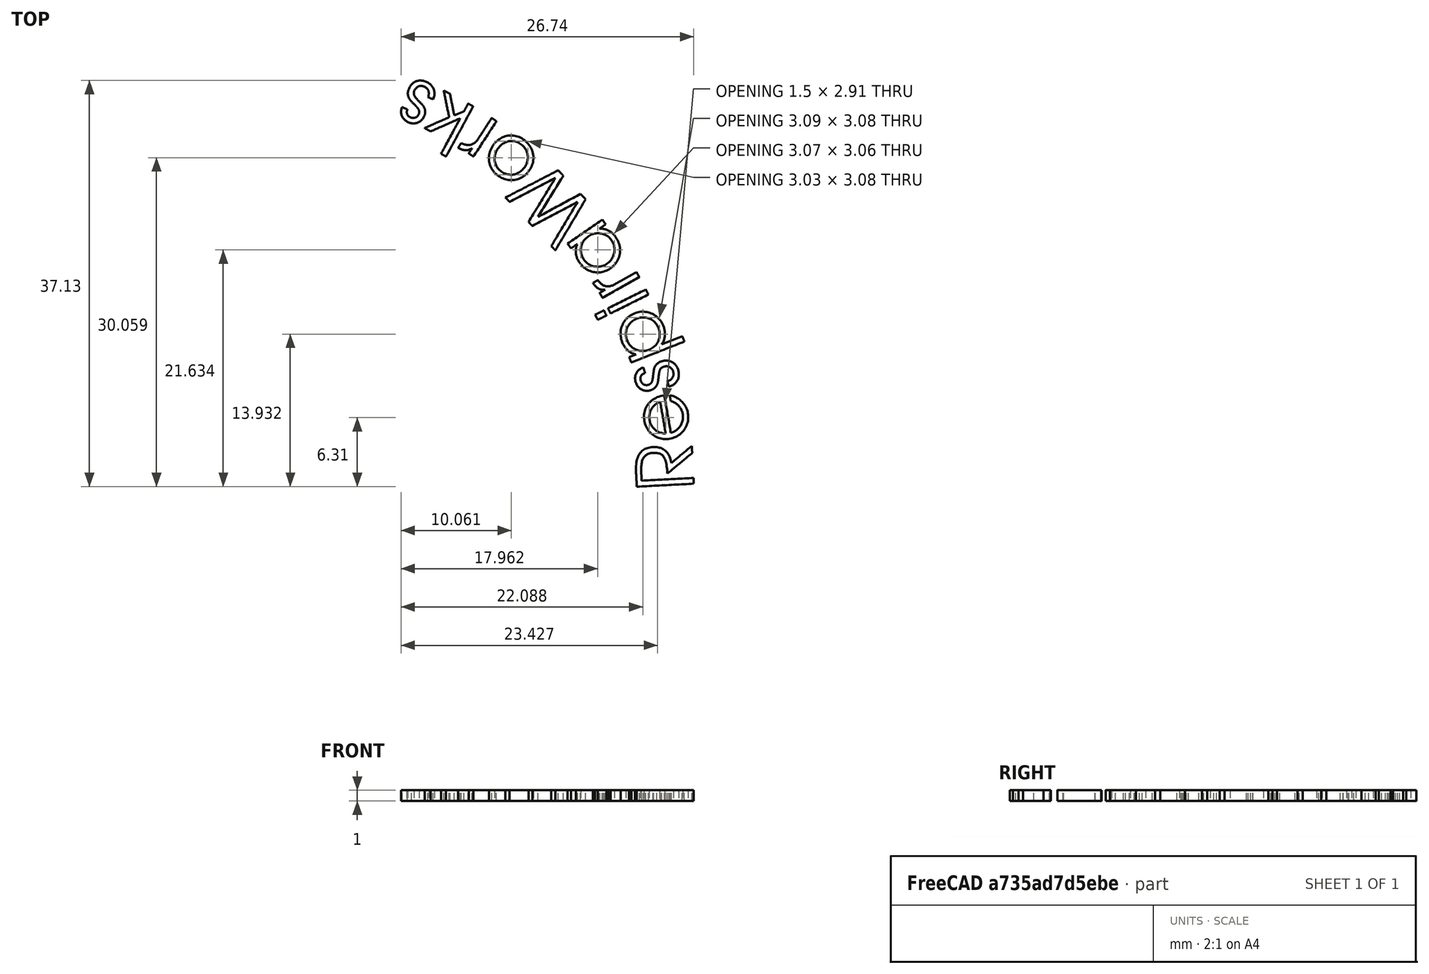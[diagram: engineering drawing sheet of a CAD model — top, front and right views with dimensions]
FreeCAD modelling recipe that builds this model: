
FCSTD DOCUMENT  (FreeCAD 0.18R4 (GitTag))
Label: RespiraWorksCircularText
License: All rights reserved
LicenseURL: http://en.wikipedia.org/wiki/All_rights_reserved
objects: Part::Feature×17, Part::Extrusion×17, Part::MultiFuse×2, Part::Cut×1
note: 37 computed .brp shape members not serialized (recipe doc carries the construction recipe); baked Part::Feature solids carry a one-line shape summary decoded from their .brp

FEATURE [Part::Feature] path1062
  shape: bbox 5.36 x 3.724 x 2e-07 mm, 0 faces, 0 solids (baked)
FEATURE [Part::Feature] path1064
  shape: bbox 4.256 x 4.117 x 2e-07 mm, 0 faces, 0 solids (baked)
FEATURE [Part::Feature] path1064001
  shape: bbox 1.557 x 2.913 x 2e-07 mm, 0 faces, 0 solids (baked)
FEATURE [Part::Feature] path1066
  shape: bbox 4.123 x 2.886 x 2e-07 mm, 0 faces, 0 solids (baked)
FEATURE [Part::Feature] path1068
  shape: bbox 5.928 x 4.739 x 2e-07 mm, 0 faces, 0 solids (baked)
FEATURE [Part::Feature] path1068001
  shape: bbox 3.237 x 3.218 x 2e-07 mm, 0 faces, 0 solids (baked)
FEATURE [Part::Feature] path1070
  shape: bbox 3.686 x 2.19 x 2e-07 mm, 0 faces, 0 solids (baked)
FEATURE [Part::Feature] path1070001
  shape: bbox 1.029 x 0.8641 x 2e-07 mm, 0 faces, 0 solids (baked)
FEATURE [Part::Feature] path1072
  shape: bbox 4.235 x 2.351 x 2e-07 mm, 0 faces, 0 solids (baked)
FEATURE [Part::Feature] path1074
  shape: bbox 4.889 x 4.925 x 2e-07 mm, 0 faces, 0 solids (baked)
FEATURE [Part::Feature] path1074001
  shape: bbox 3.229 x 3.209 x 2e-07 mm, 0 faces, 0 solids (baked)
FEATURE [Part::Feature] path1076
  shape: bbox 7.322 x 7.314 x 2e-07 mm, 0 faces, 0 solids (baked)
FEATURE [Part::Feature] path1078
  shape: bbox 4.267 x 4.276 x 2e-07 mm, 0 faces, 0 solids (baked)
FEATURE [Part::Feature] path1078001
  shape: bbox 3.195 x 3.225 x 2e-07 mm, 0 faces, 0 solids (baked)
FEATURE [Part::Feature] path1080
  shape: bbox 3.503 x 3.524 x 2e-07 mm, 0 faces, 0 solids (baked)
FEATURE [Part::Feature] path1082
  shape: bbox 4.44 x 6.043 x 2e-07 mm, 0 faces, 0 solids (baked)
FEATURE [Part::Feature] path1084
  shape: bbox 3.158 x 4.031 x 2e-07 mm, 0 faces, 0 solids (baked)
FEATURE [Part::Extrusion] Extrude
  Base = -> path1062
  Dir = (0,0,1)
  DirMode = 2
  FaceMakerClass = Part::FaceMakerBullseye
  LengthFwd = 1
  LengthRev = 0
  Solid = true
  Symmetric = false
FEATURE [Part::Extrusion] Extrude001
  Base = -> path1064
  Dir = (0,0,1)
  DirMode = 2
  FaceMakerClass = Part::FaceMakerBullseye
  LengthFwd = 1
  LengthRev = 0
  Solid = true
  Symmetric = false
FEATURE [Part::Extrusion] Extrude002
  Base = -> path1066
  Dir = (0,0,1)
  DirMode = 2
  FaceMakerClass = Part::FaceMakerBullseye
  LengthFwd = 1
  LengthRev = 0
  Solid = true
  Symmetric = false
FEATURE [Part::Extrusion] Extrude003
  Base = -> path1068
  Dir = (0,0,1)
  DirMode = 2
  FaceMakerClass = Part::FaceMakerBullseye
  LengthFwd = 1
  LengthRev = 0
  Solid = true
  Symmetric = false
FEATURE [Part::Extrusion] Extrude004
  Base = -> path1070
  Dir = (0,0,1)
  DirMode = 2
  FaceMakerClass = Part::FaceMakerBullseye
  LengthFwd = 1
  LengthRev = 0
  Solid = true
  Symmetric = false
FEATURE [Part::Extrusion] Extrude005
  Base = -> path1070001
  Dir = (0,0,1)
  DirMode = 2
  FaceMakerClass = Part::FaceMakerBullseye
  LengthFwd = 1
  LengthRev = 0
  Solid = true
  Symmetric = false
FEATURE [Part::Extrusion] Extrude006
  Base = -> path1072
  Dir = (0,0,1)
  DirMode = 2
  FaceMakerClass = Part::FaceMakerBullseye
  LengthFwd = 1
  LengthRev = 0
  Solid = true
  Symmetric = false
FEATURE [Part::Extrusion] Extrude007
  Base = -> path1074
  Dir = (0,0,1)
  DirMode = 2
  FaceMakerClass = Part::FaceMakerBullseye
  LengthFwd = 1
  LengthRev = 0
  Solid = true
  Symmetric = false
FEATURE [Part::Extrusion] Extrude008
  Base = -> path1076
  Dir = (0,0,1)
  DirMode = 2
  FaceMakerClass = Part::FaceMakerBullseye
  LengthFwd = 1
  LengthRev = 0
  Solid = true
  Symmetric = false
FEATURE [Part::Extrusion] Extrude009
  Base = -> path1078
  Dir = (0,0,1)
  DirMode = 2
  FaceMakerClass = Part::FaceMakerBullseye
  LengthFwd = 1
  LengthRev = 0
  Solid = true
  Symmetric = false
FEATURE [Part::Extrusion] Extrude010
  Base = -> path1080
  Dir = (0,0,1)
  DirMode = 2
  FaceMakerClass = Part::FaceMakerBullseye
  LengthFwd = 1
  LengthRev = 0
  Solid = true
  Symmetric = false
FEATURE [Part::Extrusion] Extrude011
  Base = -> path1082
  Dir = (0,0,1)
  DirMode = 2
  FaceMakerClass = Part::FaceMakerBullseye
  LengthFwd = 1
  LengthRev = 0
  Solid = true
  Symmetric = false
FEATURE [Part::Extrusion] Extrude012
  Base = -> path1084
  Dir = (0,0,1)
  DirMode = 2
  FaceMakerClass = Part::FaceMakerBullseye
  LengthFwd = 1
  LengthRev = 0
  Solid = true
  Symmetric = false
FEATURE [Part::MultiFuse] Fusion  label="pRespiraWorksCircularText"
  Shapes = -> [Extrude012,Extrude001,Extrude003,Extrude004,Extrude005,Extrude006,Extrude007,Extrude002,Extrude,Extrude008,Extrude011,Extrude010,Extrude009]
FEATURE [Part::Extrusion] Extrude013
  Base = -> path1064001
  Dir = (0,0,-1)
  DirMode = 2
  FaceMakerClass = Part::FaceMakerBullseye
  LengthFwd = -1
  LengthRev = 0
  Solid = true
  Symmetric = false
FEATURE [Part::Extrusion] Extrude014
  Base = -> path1068001
  Dir = (0,0,-1)
  DirMode = 2
  FaceMakerClass = Part::FaceMakerBullseye
  LengthFwd = -1
  LengthRev = 0
  Solid = true
  Symmetric = false
FEATURE [Part::Extrusion] Extrude015
  Base = -> path1074001
  Dir = (0,0,-1)
  DirMode = 2
  FaceMakerClass = Part::FaceMakerBullseye
  LengthFwd = -1
  LengthRev = 0
  Solid = true
  Symmetric = false
FEATURE [Part::Extrusion] Extrude016
  Base = -> path1078001
  Dir = (0,0,-1)
  DirMode = 2
  FaceMakerClass = Part::FaceMakerBullseye
  LengthFwd = -1
  LengthRev = 0
  Solid = true
  Symmetric = false
FEATURE [Part::MultiFuse] Fusion001  label="nRespiraWorksCircularText"
  Shapes = -> [Extrude013,Extrude015,Extrude014,Extrude016]
FEATURE [Part::Cut] Cut  label="RespiraWorksCircularText"
  Base = -> Fusion
  Tool = -> Fusion001
